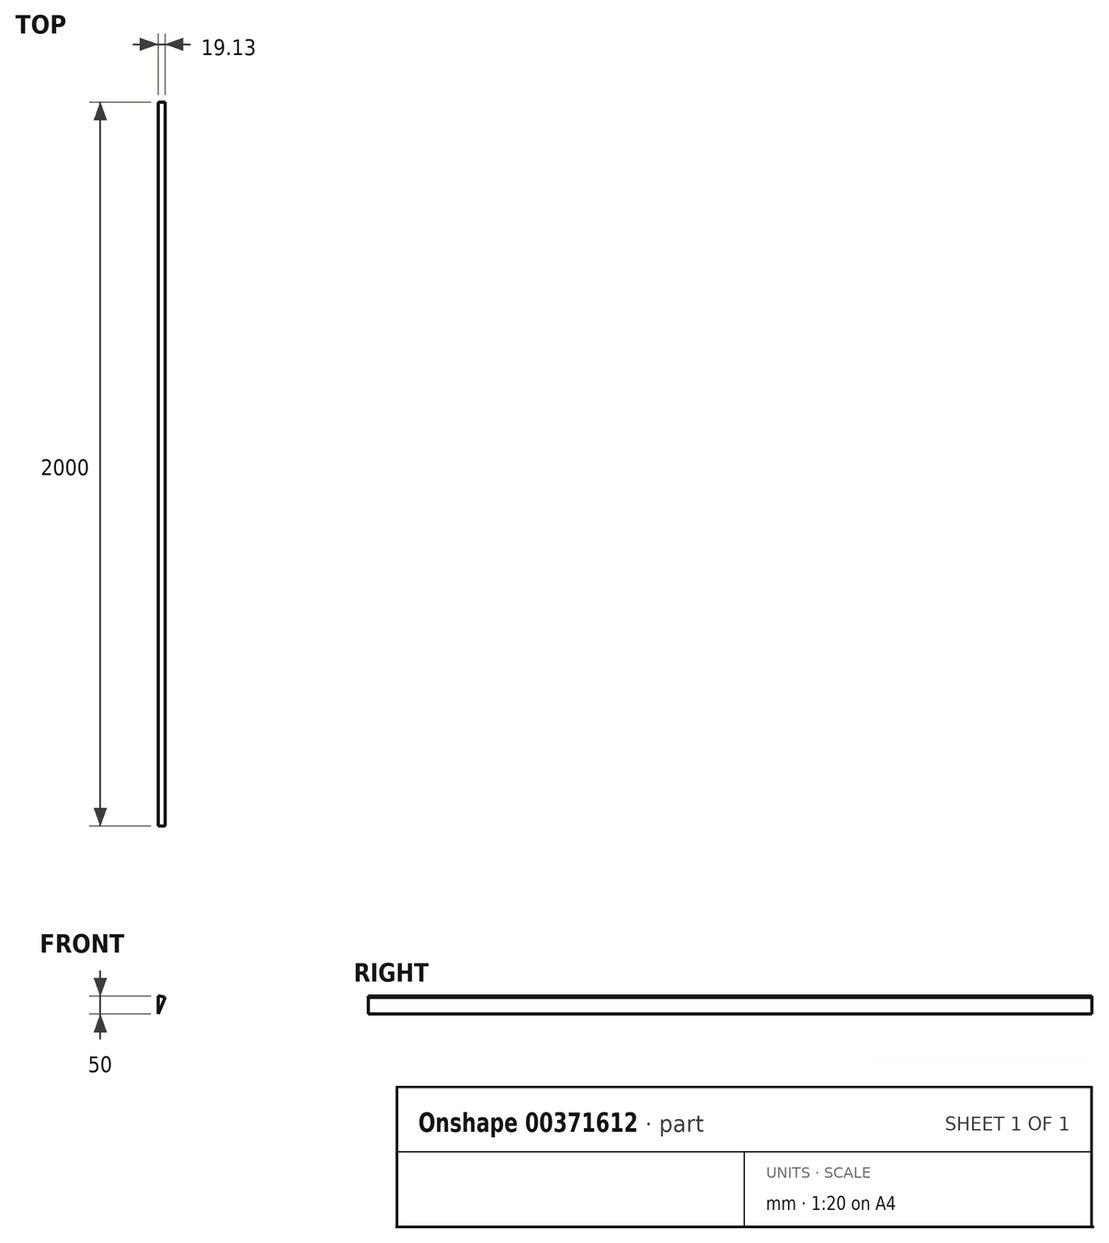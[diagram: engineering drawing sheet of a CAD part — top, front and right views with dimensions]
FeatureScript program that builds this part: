
annotation { "Feature Type Name" : "Feature", "Feature Type Description" : "" }
export const myFeature = defineFeature(function(context is Context, id is Id, definition is map)
    precondition{}
    {
        {
            var Q0;
            Q0=qCreatedBy(makeId("Front.planeOp"),FACE);
            var sketch = newSketch(context, id + "F0", { "sketchPlane" : qUnion([Q0])});
            skCircle(sketch, "E0", {"center": v(0, 0) * mm, "radius": 50 * mm});
            skLineSegment(sketch, "E1", {"start": v(0, 50) * mm, "end": v(0, 0) * mm});
            skLineSegment(sketch, "E2", {"start": v(0, 0) * mm, "end": v(19.13, 46.2) * mm});
            skSolve(sketch);
        }
        {
            var Q0;
            {var subQ0=sQuery(id+"F0.wireOp",EDGE,"E1");Q0=makeQuery(id+"F0.imprint","IMPRINT",FACE,{"disambiguationData":[TD([[makeQuery(id+"F0.imprint","IMPRINT",EDGE,{"derivedFrom":subQ0}),1.0]])]});}
            extrude(context, id + "F1", {"entities" : qUnion([Q0]), "depth" : 2000 * mm});
        }
    });
